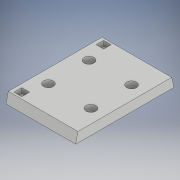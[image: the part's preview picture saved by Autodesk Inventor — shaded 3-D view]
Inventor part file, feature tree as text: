
AUTODESK INVENTOR PART (.ipt)
format: ipt  version: 2019 (Build 230136000, 136)  size: 177,664 bytes
history: native  units: in
note: dims shown in document units (in); Inventor stores cm internally (conversion verified against a paired STEP export)
features: sketch x9, plane x8, extrude x4, projected_geometry x4, hole x1, mirror x1
ambient origin geometry x8: Origin, YZ Plane, XZ Plane, XY Plane, X Axis, Y Axis, Z Axis, Center Point
bodies: Solid1 (feature_tree)
feature tree (27):
  sketch  "Sketch1"  dims[d0=0.31in d1=0.15in]
  plane  "Work Plane2"
  sketch  "Sketch2"  dims[d6=1.5in d7=0.75in]
  plane  "Work Plane4"
  sketch  "Sketch3"  dims[d8=0.15in d11=0.8125in d12=0.0in]
  plane  "Work Plane5"
  extrude  "Extrusion4"  Depth=0.15in
  plane  "Work Plane7"
  plane  "Work Plane6"
  sketch  "Sketch6"  dims[d30=0.25in d31=0.0in d35=0.8562in]
  plane  "Work Plane1"
  plane  "Work Plane3"
  extrude  "Extrusion7"  Depth=0.75in
  extrude  "Extrusion8"  Depth=0.15in TaperAngle=0.0deg
  sketch  "Sketch13"  dims[d39=0.4401in]
  plane  "Work Plane8"
  hole  "Hole2"  [1 undecoded]
  mirror  "Mirror2"
  extrude  "Extrusion9"  Depth=0.8562in
  sketch  "Sketch4"  dims[d20=0.5315in d28=0.875in d29=0.0in]
  projected_geometry  "Projected Loop1"
  sketch  "Sketch10"  dims[d36=0.8562in]
  sketch  "Sketch12"  dims[d38=0.4401in]
  projected_geometry  "Projected Loop5"
  projected_geometry  "Projected Loop6"
  projected_geometry  "Projected Loop7"
  sketch  "Sketch14"  dims[d40=0.15in d41=0.75in d42=0.375in d43=0.25in d44=0.5635in d45=1.0in d46=0.8108in d47=0.12in d48=0.12in d49=0.065in d50=0.055in d51=0.115in d52=0.115in d53=0.065in d54=0.055in d55=0.075in d56=0.0in]
note: 1 required parameter value undecoded (feature->parameter linkage not recoverable at this tier; creation-order binding heuristic only, values carry confidence <= 0.55)
